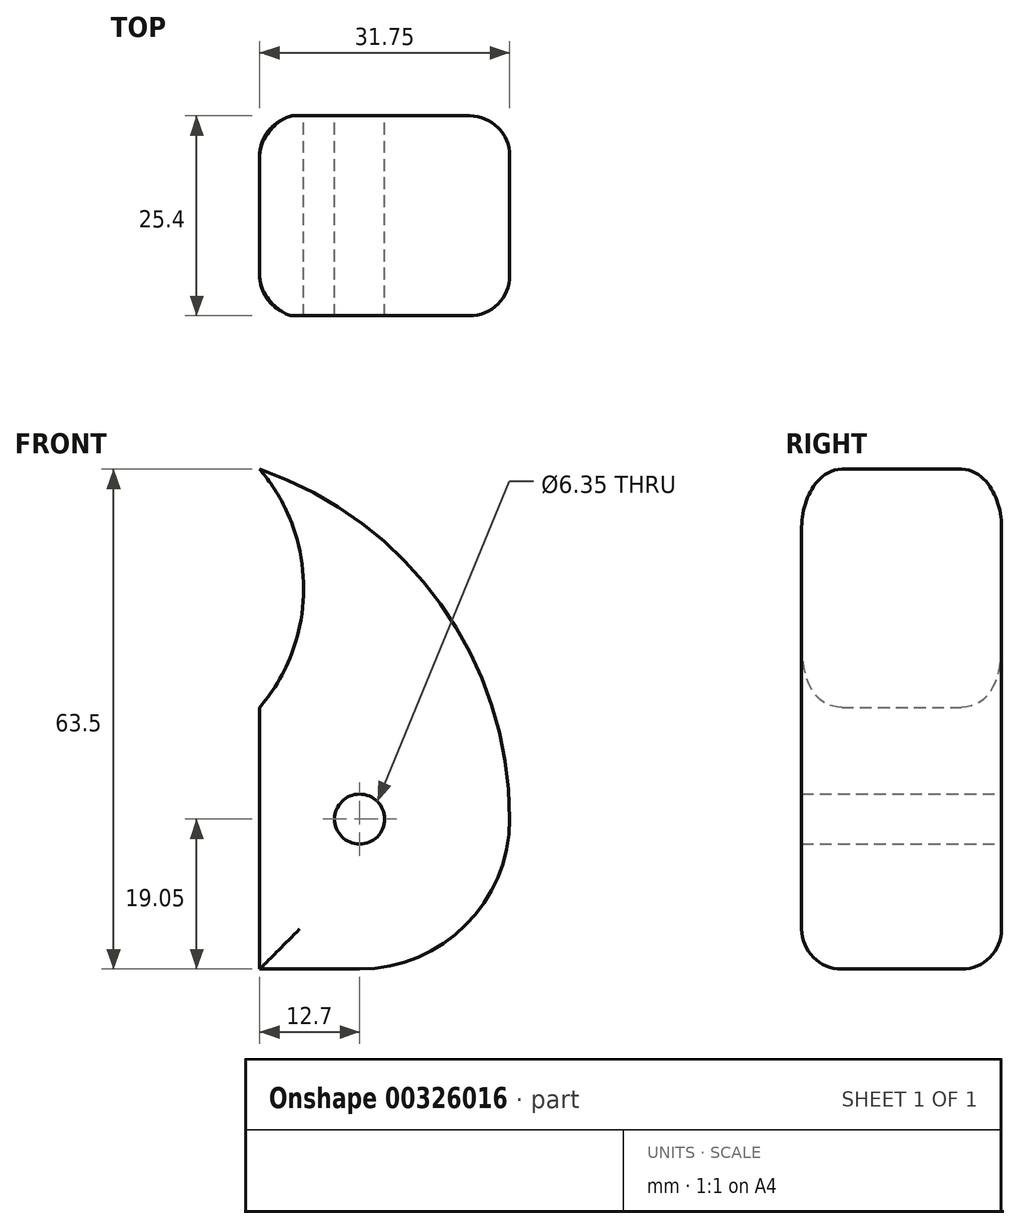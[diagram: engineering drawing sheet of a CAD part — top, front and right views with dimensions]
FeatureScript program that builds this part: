
annotation { "Feature Type Name" : "Feature", "Feature Type Description" : "" }
export const myFeature = defineFeature(function(context is Context, id is Id, definition is map)
    precondition{}
    {
        {
            var Q0;
            Q0=qCreatedBy(makeId("Front.planeOp"),FACE);
            var sketch = newSketch(context, id + "F0", { "sketchPlane" : qUnion([Q0])});
            skLineSegment(sketch, "E0.bottom", {"start": v(-19.05, 0) * mm, "end": v(-31.75, 0) * mm});
            skLineSegment(sketch, "E0.right", {"start": v(-31.75, 0) * mm, "end": v(-31.75, 33.25) * mm});
            skArc(sketch, "E1", {"start": v(-19.05, 0) * mm, "mid": v(-1.25, 25.85) * mm, "end": v(-31.75, 33.25) * mm});
            skPoint(sketch, "E2", {"position": v(-19.05, 38.1) * mm});
            skArc(sketch, "E3", {"start": v(0, 19.05) * mm, "mid": v(-8.75, 46.36) * mm, "end": v(-31.75, 63.5) * mm});
            skArc(sketch, "E4", {"start": v(-31.75, 33.25) * mm, "mid": v(-26.16, 48.37) * mm, "end": v(-31.75, 63.5) * mm});
            skCircle(sketch, "E5", {"center": v(-19.05, 19.05) * mm, "radius": 3.18 * mm});
            skSolve(sketch);
        }
        {
            var Q0;
            Q0 = qSketchRegion(id + "F0", true);
            extrude(context, id + "F1", {"entities" : qUnion([Q0]), "depth" : 25.4 * mm});
        }
        {
            var Q0;
            Q0=makeQuery(id+"F1.opExtrude","CAP_EDGE",EDGE,{"disambiguationData":[OSD([sQuery(id+"F0.wireOp",EDGE,"E0.right")])],"isStart":false});
            var Q1;
            Q1=makeQuery(id+"F1.opExtrude","CAP_EDGE",EDGE,{"disambiguationData":[OSD([sQuery(id+"F0.wireOp",EDGE,"E0.bottom")])],"isStart":false});
            fillet(context, id + "F2", {"entities" : qUnion([Q0, Q1]), "radius" : 5.08 * mm, "tangentPropagation" : true, "allowEdgeOverflow" : false});
        }
        {
            var Q0;
            Q0=makeQuery(id+"F1.opExtrude","CAP_EDGE",EDGE,{"disambiguationData":[OSD([sQuery(id+"F0.wireOp",EDGE,"E0.right")])],"isStart":true});
            var Q1;
            Q1=makeQuery(id+"F1.opExtrude","CAP_EDGE",EDGE,{"disambiguationData":[OSD([sQuery(id+"F0.wireOp",EDGE,"E0.bottom")])],"isStart":true});
            fillet(context, id + "F3", {"entities" : qUnion([Q0, Q1]), "radius" : 5.08 * mm, "tangentPropagation" : true, "allowEdgeOverflow" : false});
        }
    });
